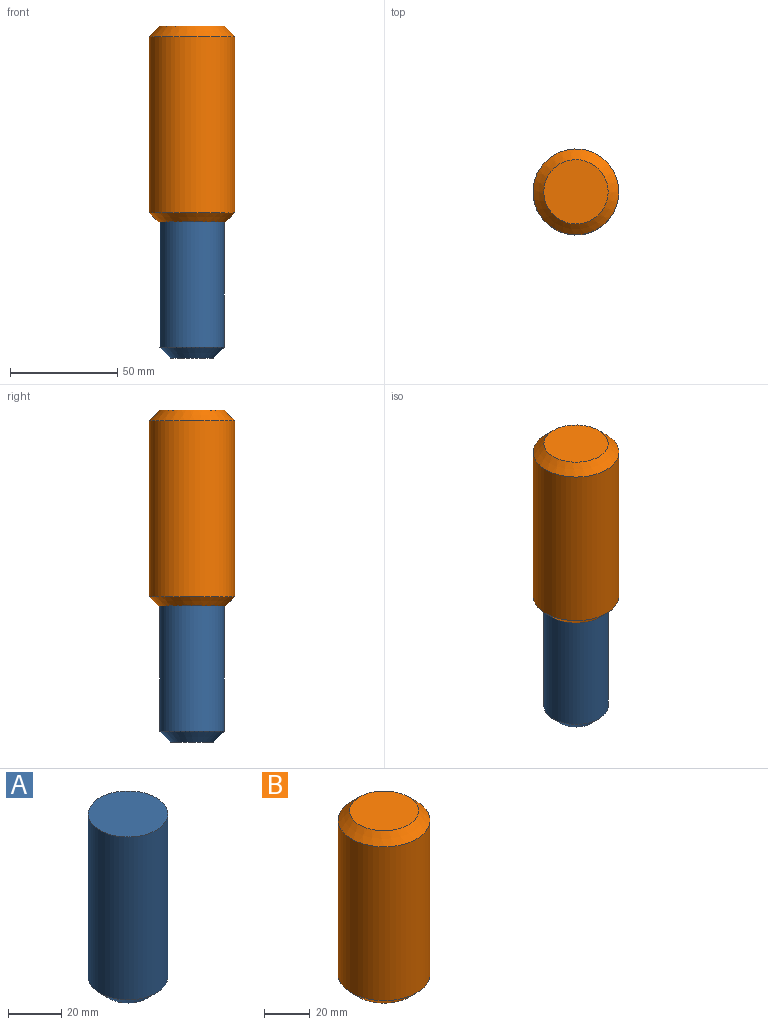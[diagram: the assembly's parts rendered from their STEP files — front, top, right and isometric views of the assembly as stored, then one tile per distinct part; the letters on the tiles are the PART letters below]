
ASSEMBLY  parts=2 mates=1
PART A: 4 faces, bbox 30x30x80 mm
  f0: cylinder r=15mm len=75mm, axis (0,0,1), area 7068.6mm2, adj f2,f3
  f1: plane 20x20mm, normal (0,0,-1), area 314.2mm2, adj f3
  f2: plane 30x30mm, normal (0,0,1), area 706.9mm2, adj f0
  f3: cone r=15mm half-angle=45deg, axis (0,0,1), area 555.4mm2, adj f0,f1
PART B: 7 faces, bbox 40x40x91.3 mm
  f0: cylinder r=20mm len=82mm, axis (0,0,-1), area 10304.4mm2, adj f4,f5
  f1: plane 30x30mm, normal (0,0,1), area 706.9mm2, adj f5
  f2: cylinder r=15mm len=79mm, axis (0,0,-1), area 7445.6mm2, adj f3,f6
  f3: plane 30x30mm, normal (0,0,-1), area 706.9mm2, adj f2
  f4: cone r=20mm half-angle=45deg, axis (0,0,1), area 681mm2, adj f0,f6
  f5: cone r=15mm half-angle=45deg, axis (0,0,-1), area 777.5mm2, adj f0,f1
  f6: cone r=15.71mm half-angle=67.5deg, axis (0,0,-1), area 73.8mm2, adj f2,f4
PLACE A t=(-7.67,-6.25,-14.23)mm fixed
PLACE B t=(-7.67,-6.25,-31.43)mm
MATE slider A.f0 <-> B.f0  axis (0,0,1) through (-7.67,-6.25,-14.23)mm
